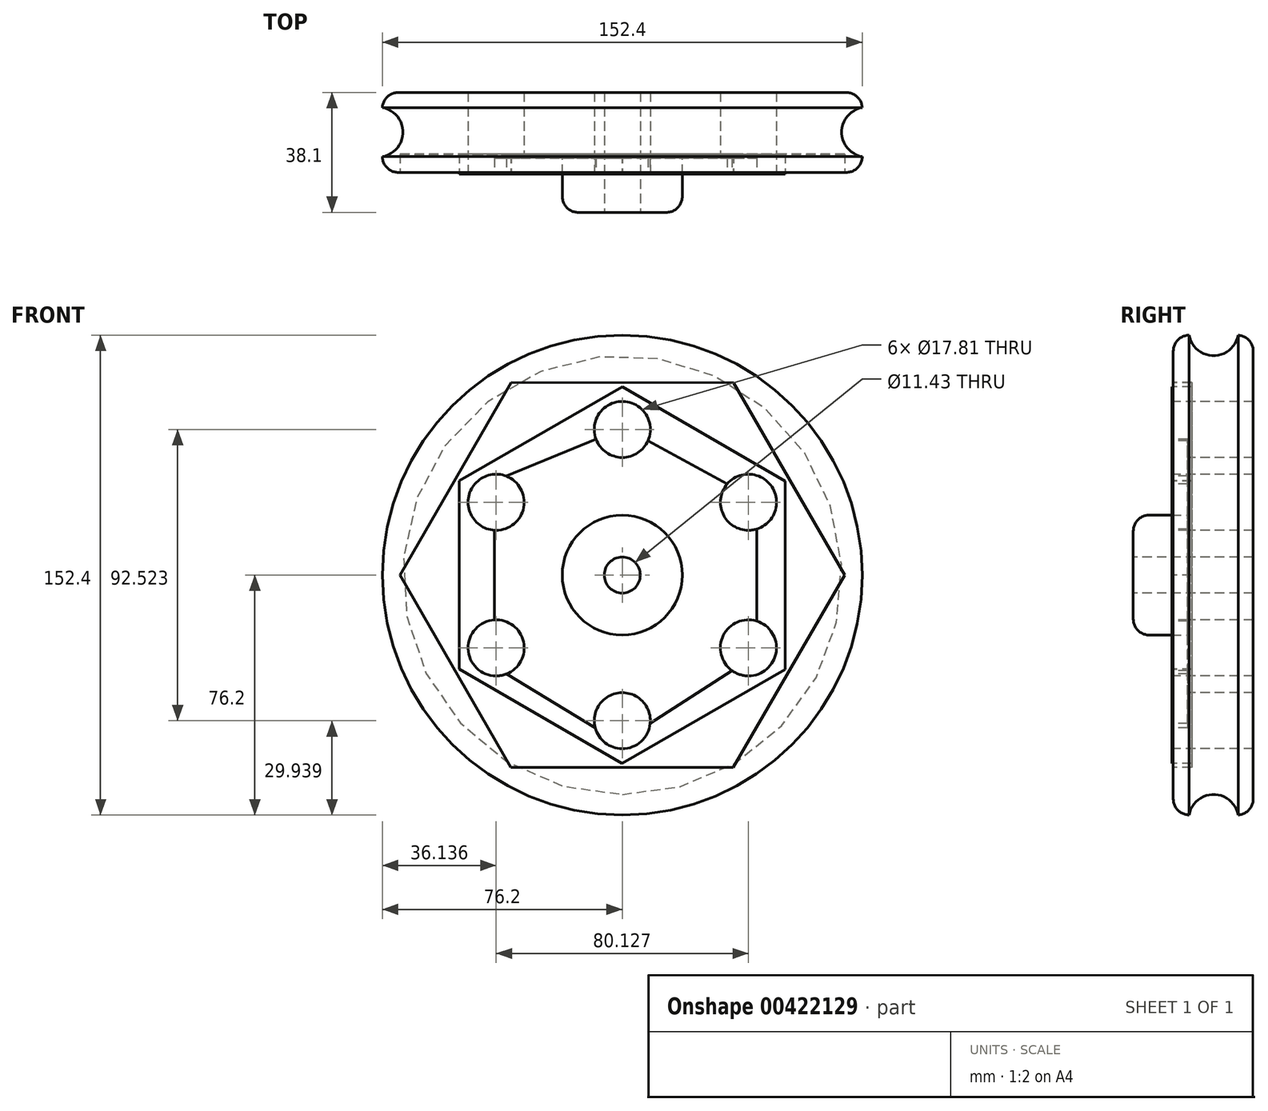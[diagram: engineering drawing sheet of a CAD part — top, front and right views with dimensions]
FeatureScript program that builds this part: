
annotation { "Feature Type Name" : "Feature", "Feature Type Description" : "" }
export const myFeature = defineFeature(function(context is Context, id is Id, definition is map)
    precondition{}
    {
        {
            var Q0;
            Q0=qCreatedBy(makeId("Front.planeOp"),FACE);
            var sketch = newSketch(context, id + "F0", { "sketchPlane" : qUnion([Q0])});
            skCircle(sketch, "E0", {"center": v(0, 0) * mm, "radius": 76.2 * mm});
            skSolve(sketch);
        }
        {
            var Q0;
            Q0 = qSketchRegion(id + "F0", true);
            extrude(context, id + "F1", {"entities" : qUnion([Q0]), "depth" : 25.4 * mm});
        }
        {
            var Q0;
            Q0=makeQuery(id+"F1.opExtrude","CAP_FACE",FACE,{"disambiguationData":[OSD([sQuery(id+"F0.wireOp",EDGE,"E0")])],"isStart":false});
            var sketch = newSketch(context, id + "F2", { "sketchPlane" : qUnion([Q0])});
            skCircle(sketch, "E1", {"center": v(0, 0) * mm, "radius": 19.05 * mm});
            skSolve(sketch);
        }
        {
            var Q0;
            Q0 = qSketchRegion(id + "F2", true);
            extrude(context, id + "F3", {"entities" : qUnion([Q0]), "operationType" : NewBodyOperationType.ADD, "depth" : 12.7 * mm});
        }
        {
            var Q0;
            Q0=makeQuery(id+"F3.opExtrude","CAP_FACE",FACE,{"disambiguationData":[OSD([sQuery(id+"F2.wireOp",EDGE,"E1")])],"isStart":false});
            var sketch = newSketch(context, id + "F4", { "sketchPlane" : qUnion([Q0])});
            skCircle(sketch, "E2", {"center": v(0, 0) * mm, "radius": 5.72 * mm});
            skSolve(sketch);
        }
        {
            var Q0;
            Q0 = qSketchRegion(id + "F4", true);
            extrude(context, id + "F5", {"entities" : qUnion([Q0]), "operationType" : NewBodyOperationType.REMOVE, "oppositeDirection" : true, "depth" : 38.1 * mm});
        }
        {
            var Q0;
            Q0=makeQuery(id+"F3.opExtrude","CAP_EDGE",EDGE,{"disambiguationData":[OSD([sQuery(id+"F2.wireOp",EDGE,"E1")])],"isStart":false});
            fillet(context, id + "F6", {"entities" : qUnion([Q0]), "radius" : 5.08 * mm, "tangentPropagation" : true, "allowEdgeOverflow" : false});
        }
        {
            var Q0;
            Q0=makeQuery(id+"F1.opExtrude","CAP_EDGE",EDGE,{"disambiguationData":[OSD([sQuery(id+"F0.wireOp",EDGE,"E0")])],"isStart":false});
            var Q1;
            Q1=makeQuery(id+"F1.opExtrude","SWEPT_FACE",FACE,{"disambiguationData":[OSD([sQuery(id+"F0.wireOp",EDGE,"E0")])]});
            fillet(context, id + "F7", {"entities" : qUnion([Q0, Q1]), "radius" : 5.08 * mm, "tangentPropagation" : true, "allowEdgeOverflow" : false});
        }
        {
            var Q0;
            Q0=qCreatedBy(makeId("Right.planeOp"),FACE);
            var sketch = newSketch(context, id + "F8", { "sketchPlane" : qUnion([Q0])});
            skCircle(sketch, "E3", {"center": v(-12.6, 77.58) * mm, "radius": 7.91 * mm});
            skPoint(sketch, "E3.first.point", {"position": v(-20.34, 75.96) * mm});
            skPoint(sketch, "E3.second.point", {"position": v(-4.85, 75.96) * mm});
            skPoint(sketch, "E3.third.point", {"position": v(-11.39, 69.76) * mm});
            skSolve(sketch);
        }
        {
            var Q0;
            Q0=makeQuery(id+"F8.imprint","IMPRINT",FACE,{"disambiguationData":[TD([[makeQuery(id+"F8.imprint","IMPRINT",EDGE,{"derivedFrom":sQuery(id+"F8.wireOp",EDGE,"E3")}),1.0]])]});
            var Q1;
            {var subQ0=sQuery(id+"F0.wireOp",EDGE,"E0");Q1=makeQuery(id+"F7.opFillet","BLEND_EDGE",EDGE,{"blendedFrom":[makeQuery(id+"F1.opExtrude","CAP_EDGE",EDGE,{"disambiguationData":[OSD([subQ0])],"isStart":false}),makeQuery(id+"F1.opExtrude","CAP_FACE",FACE,{"disambiguationData":[OSD([subQ0])],"isStart":false})],"blendedInto":[makeQuery(id+"F1.opExtrude","CAP_FACE",FACE,{"disambiguationData":[OSD([subQ0])],"isStart":false})]});}
            revolve(context, id + "F9", {"operationType" : NewBodyOperationType.REMOVE, "entities" : qUnion([Q0]), "axis" : qUnion([Q1]), "revolveType" : RevolveType.FULL, "oppositeDirection" : true});
        }
        {
            var Q0;
            Q0=makeQuery(id+"F1.opExtrude","CAP_FACE",FACE,{"disambiguationData":[OSD([sQuery(id+"F0.wireOp",EDGE,"E0")])],"isStart":false});
            var sketch = newSketch(context, id + "F10", { "sketchPlane" : qUnion([Q0])});
            skCircle(sketch, "E4.cCircle", {"center": v(0, 0) * mm, "radius": 61.13 * mm, "construction": true});
            skLineSegment(sketch, "E4.0", {"start": v(35.34, 61.11) * mm, "end": v(70.6, -0.05) * mm});
            skLineSegment(sketch, "E4.1", {"start": v(70.6, -0.05) * mm, "end": v(35.26, -61.16) * mm});
            skLineSegment(sketch, "E4.2", {"start": v(35.26, -61.16) * mm, "end": v(-35.34, -61.11) * mm});
            skLineSegment(sketch, "E4.3", {"start": v(-35.34, -61.11) * mm, "end": v(-70.6, 0.05) * mm});
            skLineSegment(sketch, "E4.4", {"start": v(-70.6, 0.05) * mm, "end": v(-35.26, 61.16) * mm});
            skLineSegment(sketch, "E4.5", {"start": v(-35.26, 61.16) * mm, "end": v(35.34, 61.11) * mm});
            skPoint(sketch, "E4.0.midPoint", {"position": v(52.96, 30.53) * mm});
            skSolve(sketch);
        }
        {
            var Q0;
            Q0 = qSketchRegion(id + "F10", true);
            extrude(context, id + "F11", {"entities" : qUnion([Q0]), "operationType" : NewBodyOperationType.ADD, "depth" : 0.5 * mm});
        }
        {
            var Q0;
            {var subQ0=sQuery(id+"F10.wireOp",EDGE,"E4.2");var subQ1=sQuery(id+"F10.wireOp",EDGE,"E4.1");var subQ2=sQuery(id+"F10.wireOp",EDGE,"E4.0");var subQ3=sQuery(id+"F10.wireOp",EDGE,"E4.3");var subQ4=sQuery(id+"F10.wireOp",EDGE,"E4.4");var subQ5=sQuery(id+"F10.wireOp",EDGE,"E4.5");Q0=makeQuery(id+"F11.boolean.opBoolean","SPLIT",FACE,{"disambiguationData":[TD([makeQuery(id+"F3.opExtrude","SWEPT_FACE",FACE,{"disambiguationData":[OSD([sQuery(id+"F2.wireOp",EDGE,"E1")])]})])],"derivedFrom":makeQuery(id+"F11.opExtrude","CAP_FACE",FACE,{"disambiguationData":[OSD([subQ2,subQ1,subQ0,subQ3,subQ4,subQ5])],"isStart":false})});}
            var sketch = newSketch(context, id + "F12", { "sketchPlane" : qUnion([Q0])});
            skCircle(sketch, "E5", {"center": v(0, 46.26) * mm, "radius": 8.9 * mm});
            skCircle(sketch, "E6.1.0", {"center": v(-40.06, 23.13) * mm, "radius": 8.9 * mm});
            skCircle(sketch, "E6.2.0", {"center": v(-40.06, -23.13) * mm, "radius": 8.9 * mm});
            skCircle(sketch, "E6.3.0", {"center": v(0, -46.26) * mm, "radius": 8.9 * mm});
            skCircle(sketch, "E6.4.0", {"center": v(40.06, -23.13) * mm, "radius": 8.9 * mm});
            skCircle(sketch, "E6.5.0", {"center": v(40.06, 23.13) * mm, "radius": 8.9 * mm});
            skPoint(sketch, "E6.center", {"position": v(0, 0) * mm});
            skSolve(sketch);
        }
        {
            var Q0;
            Q0 = qSketchRegion(id + "F12", true);
            extrude(context, id + "F13", {"entities" : qUnion([Q0]), "operationType" : NewBodyOperationType.REMOVE, "oppositeDirection" : true, "depth" : 76.2 * mm, "offsetDistance" : 25.4 * mm});
        }
        {
            var Q0;
            {var subQ0=sQuery(id+"F10.wireOp",EDGE,"E4.2");var subQ1=sQuery(id+"F10.wireOp",EDGE,"E4.1");var subQ2=sQuery(id+"F10.wireOp",EDGE,"E4.0");var subQ3=sQuery(id+"F10.wireOp",EDGE,"E4.3");var subQ4=sQuery(id+"F10.wireOp",EDGE,"E4.4");var subQ5=sQuery(id+"F10.wireOp",EDGE,"E4.5");Q0=makeQuery(id+"F11.boolean.opBoolean","SPLIT",FACE,{"disambiguationData":[TD([makeQuery(id+"F3.opExtrude","SWEPT_FACE",FACE,{"disambiguationData":[OSD([sQuery(id+"F2.wireOp",EDGE,"E1")])]})])],"derivedFrom":makeQuery(id+"F11.opExtrude","CAP_FACE",FACE,{"disambiguationData":[OSD([subQ2,subQ1,subQ0,subQ3,subQ4,subQ5])],"isStart":false})});}
            var sketch = newSketch(context, id + "F14", { "sketchPlane" : qUnion([Q0])});
            skLineSegment(sketch, "E7", {"start": v(-40.56, 14.24) * mm, "end": v(-40.56, -14.24) * mm});
            skLineSegment(sketch, "E8", {"start": v(-36.78, -31.4) * mm, "end": v(-8.6, -48.55) * mm});
            skLineSegment(sketch, "E9", {"start": v(8.86, -47.17) * mm, "end": v(34.82, -30.33) * mm});
            skLineSegment(sketch, "E10", {"start": v(42.66, -14.61) * mm, "end": v(42.66, 14.61) * mm});
            skLineSegment(sketch, "E11", {"start": v(33.28, 28.9) * mm, "end": v(8.16, 42.69) * mm});
            skLineSegment(sketch, "E12", {"start": v(-8.33, 43.11) * mm, "end": v(-36.85, 31.44) * mm});
            skSolve(sketch);
        }
        {
            var Q0;
            {var subQ0=sQuery(id+"F14.wireOp",EDGE,"E7");Q0=makeQuery(id+"F14.imprint","IMPRINT",FACE,{"disambiguationData":[TD([[makeQuery(id+"F14.imprint","IMPRINT",EDGE,{"derivedFrom":subQ0}),1.0]])]});}
            extrude(context, id + "F15", {"entities" : qUnion([Q0]), "operationType" : NewBodyOperationType.REMOVE, "oppositeDirection" : true, "depth" : 5.08 * mm, "offsetDistance" : 25.4 * mm});
        }
        {
            var Q0;
            Q0=makeQuery(id+"F11.boolean.opBoolean","SPLIT",FACE,{"disambiguationData":[TD([makeQuery(id+"F5.boolean.opBoolean","COPY",FACE,{"derivedFrom":makeQuery(id+"F5.opExtrude","SWEPT_FACE",FACE,{"disambiguationData":[OSD([sQuery(id+"F4.wireOp",EDGE,"E2")])]})})])],"derivedFrom":makeQuery(id+"F11.opExtrude","CAP_FACE",FACE,{"disambiguationData":[OSD([sQuery(id+"F10.wireOp",EDGE,"E4.0"),sQuery(id+"F10.wireOp",EDGE,"E4.1"),sQuery(id+"F10.wireOp",EDGE,"E4.2"),sQuery(id+"F10.wireOp",EDGE,"E4.3"),sQuery(id+"F10.wireOp",EDGE,"E4.4"),sQuery(id+"F10.wireOp",EDGE,"E4.5")])],"isStart":false})});
            var sketch = newSketch(context, id + "F16", { "sketchPlane" : qUnion([Q0])});
            skCircle(sketch, "E13", {"center": v(0, 0) * mm, "radius": 3.16 * mm});
            skSolve(sketch);
        }
        {
            var Q0;
            Q0=sQuery(id+"F16.wireOp",VERTEX,"E13.center");
            var Q1;
            Q1=makeQuery(id+"F1.opExtrude","SWEPT_BODY",BODY,{"disambiguationData":[OSD([sQuery(id+"F0.wireOp",EDGE,"E0")])]});
            hole(context, id + "F17", {"style" : HoleStyle.SIMPLE, "endStyle" : HoleEndStyle.THROUGH, "holeDiameter" : 11.43 * mm, "isTappedThrough" : true, "tappedDepth" : 12.7 * mm, "tapClearance" : 3, "locations" : qUnion([Q0]), "scope" : qUnion([Q1])});
        }
        {
            var Q0;
            {var subQ0=sQuery(id+"F10.wireOp",EDGE,"E4.2");var subQ1=sQuery(id+"F10.wireOp",EDGE,"E4.1");var subQ2=sQuery(id+"F10.wireOp",EDGE,"E4.0");var subQ3=sQuery(id+"F10.wireOp",EDGE,"E4.3");var subQ4=sQuery(id+"F10.wireOp",EDGE,"E4.4");var subQ5=sQuery(id+"F10.wireOp",EDGE,"E4.5");Q0=makeQuery(id+"F11.boolean.opBoolean","SPLIT",FACE,{"disambiguationData":[TD([makeQuery(id+"F3.opExtrude","SWEPT_FACE",FACE,{"disambiguationData":[OSD([sQuery(id+"F2.wireOp",EDGE,"E1")])]})])],"derivedFrom":makeQuery(id+"F11.opExtrude","CAP_FACE",FACE,{"disambiguationData":[OSD([subQ2,subQ1,subQ0,subQ3,subQ4,subQ5])],"isStart":false})});}
            var sketch = newSketch(context, id + "F18", { "sketchPlane" : qUnion([Q0])});
            skCircle(sketch, "E14.cCircle", {"center": v(0, 0) * mm, "radius": 51.76 * mm, "construction": true});
            skLineSegment(sketch, "E14.0", {"start": v(0.04, 59.77) * mm, "end": v(51.78, 29.85) * mm});
            skLineSegment(sketch, "E14.1", {"start": v(51.78, 29.85) * mm, "end": v(51.74, -29.92) * mm});
            skLineSegment(sketch, "E14.2", {"start": v(51.74, -29.92) * mm, "end": v(-0.04, -59.77) * mm});
            skLineSegment(sketch, "E14.3", {"start": v(-0.04, -59.77) * mm, "end": v(-51.78, -29.85) * mm});
            skLineSegment(sketch, "E14.4", {"start": v(-51.78, -29.85) * mm, "end": v(-51.74, 29.92) * mm});
            skLineSegment(sketch, "E14.5", {"start": v(-51.74, 29.92) * mm, "end": v(0.04, 59.77) * mm});
            skPoint(sketch, "E14.0.midPoint", {"position": v(25.91, 44.81) * mm});
            skSolve(sketch);
        }
        {
            var Q0;
            Q0=makeQuery(id+"F18.imprint","IMPRINT",FACE,{"disambiguationData":[TD([[makeQuery(id+"F18.imprint","IMPRINT",EDGE,{"derivedFrom":sQuery(id+"F18.wireOp",EDGE,"E14.0")}),1.0]])]});
            extrude(context, id + "F19", {"entities" : qUnion([Q0]), "operationType" : NewBodyOperationType.REMOVE, "oppositeDirection" : true, "depth" : 6.35 * mm, "offsetDistance" : 25.4 * mm});
        }
    });
